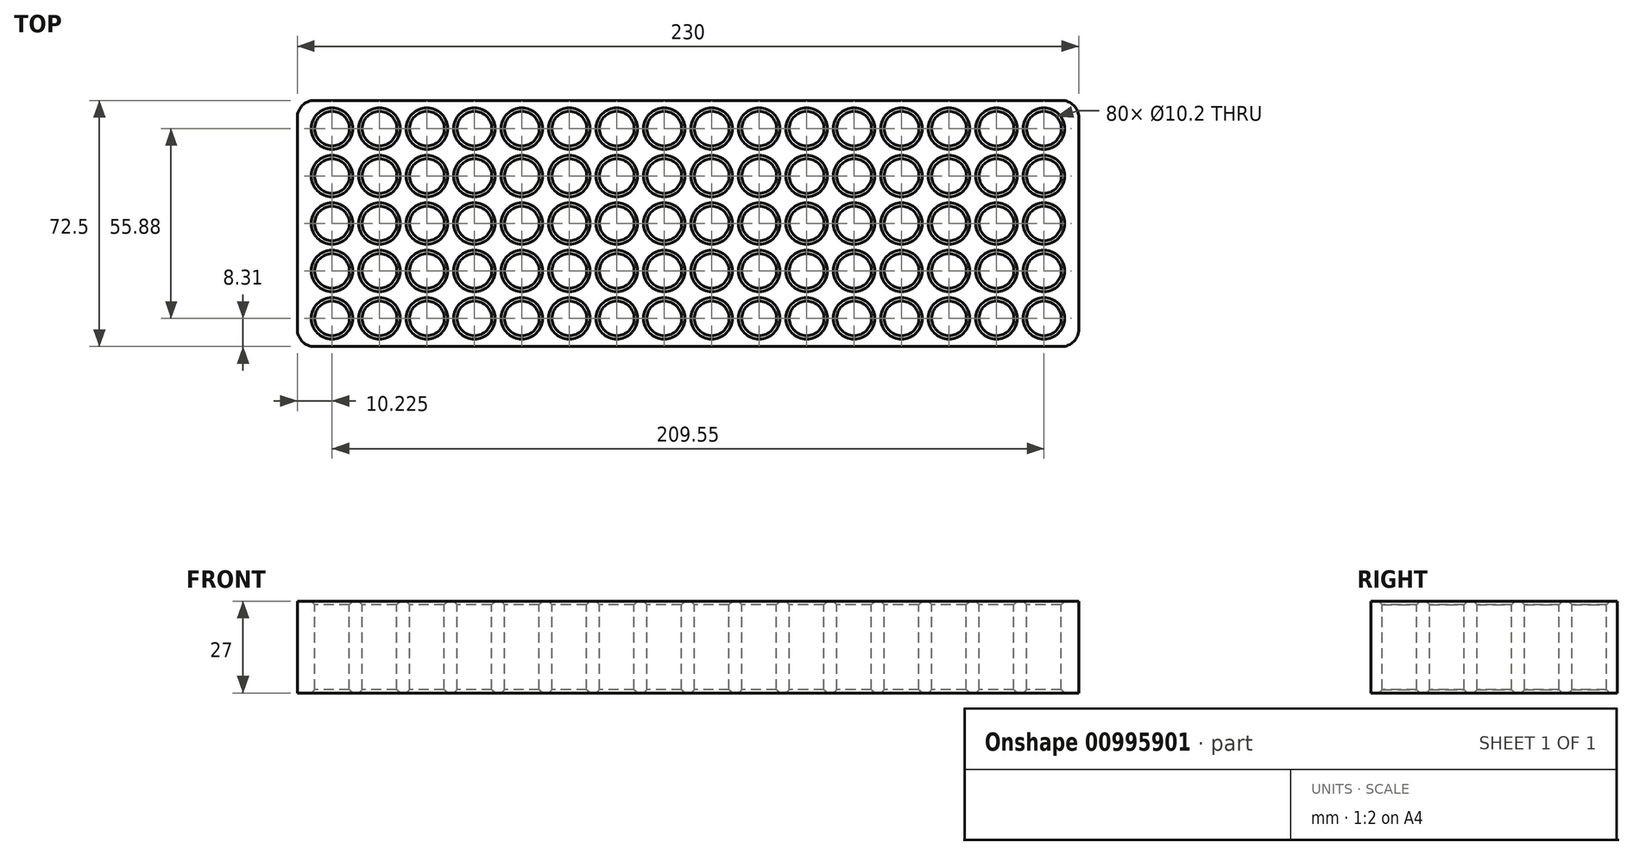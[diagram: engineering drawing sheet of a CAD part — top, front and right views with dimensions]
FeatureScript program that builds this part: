
annotation { "Feature Type Name" : "Feature", "Feature Type Description" : "" }
export const myFeature = defineFeature(function(context is Context, id is Id, definition is map)
    precondition{}
    {
        {
            var Q0;
            Q0=qCreatedBy(makeId("Top.planeOp"),FACE);
            var sketch = newSketch(context, id + "F0", { "sketchPlane" : qUnion([Q0])});
            skLineSegment(sketch, "E0.bottom", {"start": v(115, 36.25) * mm, "end": v(-115, 36.25) * mm});
            skLineSegment(sketch, "E0.top", {"start": v(115, -36.25) * mm, "end": v(-115, -36.25) * mm});
            skLineSegment(sketch, "E0.left", {"start": v(115, 36.25) * mm, "end": v(115, -36.25) * mm});
            skLineSegment(sketch, "E0.right", {"start": v(-115, 36.25) * mm, "end": v(-115, -36.25) * mm});
            skPoint(sketch, "E0.middle", {"position": v(0, 0) * mm});
            skSolve(sketch);
        }
        {
            var Q0;
            Q0=makeQuery(id+"F0.imprint","IMPRINT",FACE,{"disambiguationData":[TD([[makeQuery(id+"F0.imprint","IMPRINT",EDGE,{"derivedFrom":sQuery(id+"F0.wireOp",EDGE,"E0.bottom")}),1.0]])]});
            extrude(context, id + "F1", {"entities" : qUnion([Q0]), "endBound" : BoundingType.SYMMETRIC, "depth" : 27 * mm, "offsetDistance" : 25.4 * mm});
        }
        {
            var Q0;
            Q0=makeQuery(id+"F1.opExtrude","CAP_FACE",FACE,{"disambiguationData":[OSD([sQuery(id+"F0.wireOp",EDGE,"E0.bottom"),sQuery(id+"F0.wireOp",EDGE,"E0.top"),sQuery(id+"F0.wireOp",EDGE,"E0.left"),sQuery(id+"F0.wireOp",EDGE,"E0.right")])],"isStart":false});
            var sketch = newSketch(context, id + "F2", { "sketchPlane" : qUnion([Q0])});
            skCircle(sketch, "E1", {"center": v(-104.78, 27.94) * mm, "radius": 5.1 * mm});
            skCircle(sketch, "E2.0.1.0", {"center": v(-104.78, 13.97) * mm, "radius": 5.1 * mm});
            skCircle(sketch, "E2.0.2.0", {"center": v(-104.77, 0) * mm, "radius": 5.1 * mm});
            skCircle(sketch, "E2.0.3.0", {"center": v(-104.78, -13.97) * mm, "radius": 5.1 * mm});
            skCircle(sketch, "E2.0.4.0", {"center": v(-104.78, -27.94) * mm, "radius": 5.1 * mm});
            skCircle(sketch, "E2.1.0.0", {"center": v(-90.8, 27.94) * mm, "radius": 5.1 * mm});
            skCircle(sketch, "E2.1.1.0", {"center": v(-90.8, 13.97) * mm, "radius": 5.1 * mm});
            skCircle(sketch, "E2.1.2.0", {"center": v(-90.8, 0) * mm, "radius": 5.1 * mm});
            skCircle(sketch, "E2.1.3.0", {"center": v(-90.8, -13.97) * mm, "radius": 5.1 * mm});
            skCircle(sketch, "E2.1.4.0", {"center": v(-90.8, -27.94) * mm, "radius": 5.1 * mm});
            skCircle(sketch, "E2.2.0.0", {"center": v(-76.84, 27.94) * mm, "radius": 5.1 * mm});
            skCircle(sketch, "E2.2.1.0", {"center": v(-76.84, 13.97) * mm, "radius": 5.1 * mm});
            skCircle(sketch, "E2.2.2.0", {"center": v(-76.83, 0) * mm, "radius": 5.1 * mm});
            skCircle(sketch, "E2.2.3.0", {"center": v(-76.84, -13.97) * mm, "radius": 5.1 * mm});
            skCircle(sketch, "E2.2.4.0", {"center": v(-76.84, -27.94) * mm, "radius": 5.1 * mm});
            skCircle(sketch, "E2.3.0.0", {"center": v(-62.87, 27.94) * mm, "radius": 5.1 * mm});
            skCircle(sketch, "E2.3.1.0", {"center": v(-62.87, 13.97) * mm, "radius": 5.1 * mm});
            skCircle(sketch, "E2.3.2.0", {"center": v(-62.87, 0) * mm, "radius": 5.1 * mm});
            skCircle(sketch, "E2.3.3.0", {"center": v(-62.87, -13.97) * mm, "radius": 5.1 * mm});
            skCircle(sketch, "E2.3.4.0", {"center": v(-62.87, -27.94) * mm, "radius": 5.1 * mm});
            skCircle(sketch, "E2.4.0.0", {"center": v(-48.9, 27.94) * mm, "radius": 5.1 * mm});
            skCircle(sketch, "E2.4.1.0", {"center": v(-48.9, 13.97) * mm, "radius": 5.1 * mm});
            skCircle(sketch, "E2.4.2.0", {"center": v(-48.9, 0) * mm, "radius": 5.1 * mm});
            skCircle(sketch, "E2.4.3.0", {"center": v(-48.9, -13.97) * mm, "radius": 5.1 * mm});
            skCircle(sketch, "E2.4.4.0", {"center": v(-48.9, -27.94) * mm, "radius": 5.1 * mm});
            skCircle(sketch, "E2.5.0.0", {"center": v(-34.93, 27.94) * mm, "radius": 5.1 * mm});
            skCircle(sketch, "E2.5.1.0", {"center": v(-34.93, 13.97) * mm, "radius": 5.1 * mm});
            skCircle(sketch, "E2.5.2.0", {"center": v(-34.93, 0) * mm, "radius": 5.1 * mm});
            skCircle(sketch, "E2.5.3.0", {"center": v(-34.93, -13.97) * mm, "radius": 5.1 * mm});
            skCircle(sketch, "E2.5.4.0", {"center": v(-34.93, -27.94) * mm, "radius": 5.1 * mm});
            skCircle(sketch, "E2.6.0.0", {"center": v(-20.96, 27.94) * mm, "radius": 5.1 * mm});
            skCircle(sketch, "E2.6.1.0", {"center": v(-20.96, 13.97) * mm, "radius": 5.1 * mm});
            skCircle(sketch, "E2.6.2.0", {"center": v(-20.96, 0) * mm, "radius": 5.1 * mm});
            skCircle(sketch, "E2.6.3.0", {"center": v(-20.96, -13.97) * mm, "radius": 5.1 * mm});
            skCircle(sketch, "E2.6.4.0", {"center": v(-20.96, -27.94) * mm, "radius": 5.1 * mm});
            skCircle(sketch, "E2.7.0.0", {"center": v(-6.99, 27.94) * mm, "radius": 5.1 * mm});
            skCircle(sketch, "E2.7.1.0", {"center": v(-6.99, 13.97) * mm, "radius": 5.1 * mm});
            skCircle(sketch, "E2.7.2.0", {"center": v(-6.99, 0) * mm, "radius": 5.1 * mm});
            skCircle(sketch, "E2.7.3.0", {"center": v(-6.99, -13.97) * mm, "radius": 5.1 * mm});
            skCircle(sketch, "E2.7.4.0", {"center": v(-6.99, -27.94) * mm, "radius": 5.1 * mm});
            skCircle(sketch, "E2.8.0.0", {"center": v(6.98, 27.94) * mm, "radius": 5.1 * mm});
            skCircle(sketch, "E2.8.1.0", {"center": v(6.98, 13.97) * mm, "radius": 5.1 * mm});
            skCircle(sketch, "E2.8.2.0", {"center": v(6.98, 0) * mm, "radius": 5.1 * mm});
            skCircle(sketch, "E2.8.3.0", {"center": v(6.98, -13.97) * mm, "radius": 5.1 * mm});
            skCircle(sketch, "E2.8.4.0", {"center": v(6.98, -27.94) * mm, "radius": 5.1 * mm});
            skCircle(sketch, "E2.9.0.0", {"center": v(20.96, 27.94) * mm, "radius": 5.1 * mm});
            skCircle(sketch, "E2.9.1.0", {"center": v(20.96, 13.97) * mm, "radius": 5.1 * mm});
            skCircle(sketch, "E2.9.2.0", {"center": v(20.95, 0) * mm, "radius": 5.1 * mm});
            skCircle(sketch, "E2.9.3.0", {"center": v(20.96, -13.97) * mm, "radius": 5.1 * mm});
            skCircle(sketch, "E2.9.4.0", {"center": v(20.96, -27.94) * mm, "radius": 5.1 * mm});
            skCircle(sketch, "E2.10.0.0", {"center": v(34.93, 27.94) * mm, "radius": 5.1 * mm});
            skCircle(sketch, "E2.10.1.0", {"center": v(34.93, 13.97) * mm, "radius": 5.1 * mm});
            skCircle(sketch, "E2.10.2.0", {"center": v(34.92, 0) * mm, "radius": 5.1 * mm});
            skCircle(sketch, "E2.10.3.0", {"center": v(34.93, -13.97) * mm, "radius": 5.1 * mm});
            skCircle(sketch, "E2.10.4.0", {"center": v(34.93, -27.94) * mm, "radius": 5.1 * mm});
            skCircle(sketch, "E2.11.0.0", {"center": v(48.9, 27.94) * mm, "radius": 5.1 * mm});
            skCircle(sketch, "E2.11.1.0", {"center": v(48.9, 13.97) * mm, "radius": 5.1 * mm});
            skCircle(sketch, "E2.11.2.0", {"center": v(48.9, 0) * mm, "radius": 5.1 * mm});
            skCircle(sketch, "E2.11.3.0", {"center": v(48.9, -13.97) * mm, "radius": 5.1 * mm});
            skCircle(sketch, "E2.11.4.0", {"center": v(48.9, -27.94) * mm, "radius": 5.1 * mm});
            skCircle(sketch, "E2.12.0.0", {"center": v(62.87, 27.94) * mm, "radius": 5.1 * mm});
            skCircle(sketch, "E2.12.1.0", {"center": v(62.87, 13.97) * mm, "radius": 5.1 * mm});
            skCircle(sketch, "E2.12.2.0", {"center": v(62.86, 0) * mm, "radius": 5.1 * mm});
            skCircle(sketch, "E2.12.3.0", {"center": v(62.87, -13.97) * mm, "radius": 5.1 * mm});
            skCircle(sketch, "E2.12.4.0", {"center": v(62.87, -27.94) * mm, "radius": 5.1 * mm});
            skCircle(sketch, "E2.13.0.0", {"center": v(76.84, 27.94) * mm, "radius": 5.1 * mm});
            skCircle(sketch, "E2.13.1.0", {"center": v(76.84, 13.97) * mm, "radius": 5.1 * mm});
            skCircle(sketch, "E2.13.2.0", {"center": v(76.83, 0) * mm, "radius": 5.1 * mm});
            skCircle(sketch, "E2.13.3.0", {"center": v(76.84, -13.97) * mm, "radius": 5.1 * mm});
            skCircle(sketch, "E2.13.4.0", {"center": v(76.84, -27.94) * mm, "radius": 5.1 * mm});
            skCircle(sketch, "E2.14.0.0", {"center": v(90.8, 27.94) * mm, "radius": 5.1 * mm});
            skCircle(sketch, "E2.14.1.0", {"center": v(90.8, 13.97) * mm, "radius": 5.1 * mm});
            skCircle(sketch, "E2.14.2.0", {"center": v(90.8, 0) * mm, "radius": 5.1 * mm});
            skCircle(sketch, "E2.14.3.0", {"center": v(90.8, -13.97) * mm, "radius": 5.1 * mm});
            skCircle(sketch, "E2.14.4.0", {"center": v(90.8, -27.94) * mm, "radius": 5.1 * mm});
            skCircle(sketch, "E2.15.0.0", {"center": v(104.78, 27.94) * mm, "radius": 5.1 * mm});
            skCircle(sketch, "E2.15.1.0", {"center": v(104.78, 13.97) * mm, "radius": 5.1 * mm});
            skCircle(sketch, "E2.15.2.0", {"center": v(104.77, 0) * mm, "radius": 5.1 * mm});
            skCircle(sketch, "E2.15.3.0", {"center": v(104.78, -13.97) * mm, "radius": 5.1 * mm});
            skCircle(sketch, "E2.15.4.0", {"center": v(104.78, -27.94) * mm, "radius": 5.1 * mm});
            skLineSegment(sketch, "E2.direction1", {"start": v(-104.78, 27.94) * mm, "end": v(-90.8, 27.94) * mm, "construction": true});
            skLineSegment(sketch, "E2.direction2", {"start": v(-104.78, 27.94) * mm, "end": v(-104.78, 13.97) * mm, "construction": true});
            skSolve(sketch);
        }
        {
            var Q0;
            Q0 = qSketchRegion(id + "F2", true);
            extrude(context, id + "F3", {"entities" : qUnion([Q0]), "operationType" : NewBodyOperationType.REMOVE, "endBound" : BoundingType.THROUGH_ALL, "oppositeDirection" : true, "depth" : 25.4 * mm, "offsetDistance" : 25.4 * mm});
        }
        {
            var Q0;
            Q0=makeQuery(id+"F3.boolean.opBoolean","COPY",FACE,{"derivedFrom":makeQuery(id+"F3.opExtrude","SWEPT_FACE",FACE,{"disambiguationData":[OSD([sQuery(id+"F2.wireOp",EDGE,"E1")])]})});
            var Q1;
            Q1=makeQuery(id+"F3.boolean.opBoolean","COPY",FACE,{"derivedFrom":makeQuery(id+"F3.opExtrude","SWEPT_FACE",FACE,{"disambiguationData":[OSD([sQuery(id+"F2.wireOp",EDGE,"E2.0.1.0")])]})});
            var Q2;
            Q2=makeQuery(id+"F3.boolean.opBoolean","COPY",FACE,{"derivedFrom":makeQuery(id+"F3.opExtrude","SWEPT_FACE",FACE,{"disambiguationData":[OSD([sQuery(id+"F2.wireOp",EDGE,"E2.1.0.0")])]})});
            var Q3;
            Q3=makeQuery(id+"F3.boolean.opBoolean","COPY",FACE,{"derivedFrom":makeQuery(id+"F3.opExtrude","SWEPT_FACE",FACE,{"disambiguationData":[OSD([sQuery(id+"F2.wireOp",EDGE,"E2.1.1.0")])]})});
            var Q4;
            Q4=makeQuery(id+"F3.boolean.opBoolean","COPY",FACE,{"derivedFrom":makeQuery(id+"F3.opExtrude","SWEPT_FACE",FACE,{"disambiguationData":[OSD([sQuery(id+"F2.wireOp",EDGE,"E2.2.0.0")])]})});
            var Q5;
            Q5=makeQuery(id+"F3.boolean.opBoolean","COPY",FACE,{"derivedFrom":makeQuery(id+"F3.opExtrude","SWEPT_FACE",FACE,{"disambiguationData":[OSD([sQuery(id+"F2.wireOp",EDGE,"E2.3.0.0")])]})});
            var Q6;
            Q6=makeQuery(id+"F3.boolean.opBoolean","COPY",FACE,{"derivedFrom":makeQuery(id+"F3.opExtrude","SWEPT_FACE",FACE,{"disambiguationData":[OSD([sQuery(id+"F2.wireOp",EDGE,"E2.4.0.0")])]})});
            var Q7;
            Q7=makeQuery(id+"F3.boolean.opBoolean","COPY",FACE,{"derivedFrom":makeQuery(id+"F3.opExtrude","SWEPT_FACE",FACE,{"disambiguationData":[OSD([sQuery(id+"F2.wireOp",EDGE,"E2.2.1.0")])]})});
            var Q8;
            Q8=makeQuery(id+"F3.boolean.opBoolean","COPY",FACE,{"derivedFrom":makeQuery(id+"F3.opExtrude","SWEPT_FACE",FACE,{"disambiguationData":[OSD([sQuery(id+"F2.wireOp",EDGE,"E2.2.2.0")])]})});
            var Q9;
            Q9=makeQuery(id+"F3.boolean.opBoolean","COPY",FACE,{"derivedFrom":makeQuery(id+"F3.opExtrude","SWEPT_FACE",FACE,{"disambiguationData":[OSD([sQuery(id+"F2.wireOp",EDGE,"E2.2.3.0")])]})});
            var Q10;
            Q10=makeQuery(id+"F3.boolean.opBoolean","COPY",FACE,{"derivedFrom":makeQuery(id+"F3.opExtrude","SWEPT_FACE",FACE,{"disambiguationData":[OSD([sQuery(id+"F2.wireOp",EDGE,"E2.2.4.0")])]})});
            var Q11;
            Q11=makeQuery(id+"F3.boolean.opBoolean","COPY",FACE,{"derivedFrom":makeQuery(id+"F3.opExtrude","SWEPT_FACE",FACE,{"disambiguationData":[OSD([sQuery(id+"F2.wireOp",EDGE,"E2.3.4.0")])]})});
            var Q12;
            Q12=makeQuery(id+"F3.boolean.opBoolean","COPY",FACE,{"derivedFrom":makeQuery(id+"F3.opExtrude","SWEPT_FACE",FACE,{"disambiguationData":[OSD([sQuery(id+"F2.wireOp",EDGE,"E2.3.3.0")])]})});
            var Q13;
            Q13=makeQuery(id+"F3.boolean.opBoolean","COPY",FACE,{"derivedFrom":makeQuery(id+"F3.opExtrude","SWEPT_FACE",FACE,{"disambiguationData":[OSD([sQuery(id+"F2.wireOp",EDGE,"E2.3.2.0")])]})});
            var Q14;
            Q14=makeQuery(id+"F3.boolean.opBoolean","COPY",FACE,{"derivedFrom":makeQuery(id+"F3.opExtrude","SWEPT_FACE",FACE,{"disambiguationData":[OSD([sQuery(id+"F2.wireOp",EDGE,"E2.3.1.0")])]})});
            var Q15;
            Q15=makeQuery(id+"F3.boolean.opBoolean","COPY",FACE,{"derivedFrom":makeQuery(id+"F3.opExtrude","SWEPT_FACE",FACE,{"disambiguationData":[OSD([sQuery(id+"F2.wireOp",EDGE,"E2.4.2.0")])]})});
            var Q16;
            Q16=makeQuery(id+"F3.boolean.opBoolean","COPY",FACE,{"derivedFrom":makeQuery(id+"F3.opExtrude","SWEPT_FACE",FACE,{"disambiguationData":[OSD([sQuery(id+"F2.wireOp",EDGE,"E2.4.3.0")])]})});
            var Q17;
            Q17=makeQuery(id+"F3.boolean.opBoolean","COPY",FACE,{"derivedFrom":makeQuery(id+"F3.opExtrude","SWEPT_FACE",FACE,{"disambiguationData":[OSD([sQuery(id+"F2.wireOp",EDGE,"E2.4.4.0")])]})});
            var Q18;
            Q18=makeQuery(id+"F3.boolean.opBoolean","COPY",FACE,{"derivedFrom":makeQuery(id+"F3.opExtrude","SWEPT_FACE",FACE,{"disambiguationData":[OSD([sQuery(id+"F2.wireOp",EDGE,"E2.4.1.0")])]})});
            var Q19;
            Q19=makeQuery(id+"F3.boolean.opBoolean","COPY",FACE,{"derivedFrom":makeQuery(id+"F3.opExtrude","SWEPT_FACE",FACE,{"disambiguationData":[OSD([sQuery(id+"F2.wireOp",EDGE,"E2.5.1.0")])]})});
            var Q20;
            Q20=makeQuery(id+"F3.boolean.opBoolean","COPY",FACE,{"derivedFrom":makeQuery(id+"F3.opExtrude","SWEPT_FACE",FACE,{"disambiguationData":[OSD([sQuery(id+"F2.wireOp",EDGE,"E2.5.0.0")])]})});
            var Q21;
            Q21=makeQuery(id+"F3.boolean.opBoolean","COPY",EDGE,{"derivedFrom":makeQuery(id+"F3.opExtrude","CAP_EDGE",EDGE,{"disambiguationData":[OSD([sQuery(id+"F2.wireOp",EDGE,"E2.6.0.0")])],"isStart":true})});
            var Q22;
            Q22=makeQuery(id+"F3.boolean.opBoolean","COPY",FACE,{"derivedFrom":makeQuery(id+"F3.opExtrude","SWEPT_FACE",FACE,{"disambiguationData":[OSD([sQuery(id+"F2.wireOp",EDGE,"E2.6.1.0")])]})});
            var Q23;
            Q23=makeQuery(id+"F3.boolean.opBoolean","COPY",FACE,{"derivedFrom":makeQuery(id+"F3.opExtrude","SWEPT_FACE",FACE,{"disambiguationData":[OSD([sQuery(id+"F2.wireOp",EDGE,"E2.6.0.0")])]})});
            var Q24;
            Q24=makeQuery(id+"F3.boolean.opBoolean","COPY",FACE,{"derivedFrom":makeQuery(id+"F3.opExtrude","SWEPT_FACE",FACE,{"disambiguationData":[OSD([sQuery(id+"F2.wireOp",EDGE,"E2.6.2.0")])]})});
            var Q25;
            Q25=makeQuery(id+"F3.boolean.opBoolean","COPY",FACE,{"derivedFrom":makeQuery(id+"F3.opExtrude","SWEPT_FACE",FACE,{"disambiguationData":[OSD([sQuery(id+"F2.wireOp",EDGE,"E2.5.2.0")])]})});
            var Q26;
            Q26=makeQuery(id+"F3.boolean.opBoolean","COPY",FACE,{"derivedFrom":makeQuery(id+"F3.opExtrude","SWEPT_FACE",FACE,{"disambiguationData":[OSD([sQuery(id+"F2.wireOp",EDGE,"E2.5.3.0")])]})});
            var Q27;
            Q27=makeQuery(id+"F3.boolean.opBoolean","COPY",FACE,{"derivedFrom":makeQuery(id+"F3.opExtrude","SWEPT_FACE",FACE,{"disambiguationData":[OSD([sQuery(id+"F2.wireOp",EDGE,"E2.6.3.0")])]})});
            var Q28;
            Q28=makeQuery(id+"F3.boolean.opBoolean","COPY",FACE,{"derivedFrom":makeQuery(id+"F3.opExtrude","SWEPT_FACE",FACE,{"disambiguationData":[OSD([sQuery(id+"F2.wireOp",EDGE,"E2.5.4.0")])]})});
            var Q29;
            Q29=makeQuery(id+"F3.boolean.opBoolean","COPY",FACE,{"derivedFrom":makeQuery(id+"F3.opExtrude","SWEPT_FACE",FACE,{"disambiguationData":[OSD([sQuery(id+"F2.wireOp",EDGE,"E2.6.4.0")])]})});
            var Q30;
            Q30=makeQuery(id+"F3.boolean.opBoolean","COPY",FACE,{"derivedFrom":makeQuery(id+"F3.opExtrude","SWEPT_FACE",FACE,{"disambiguationData":[OSD([sQuery(id+"F2.wireOp",EDGE,"E2.7.4.0")])]})});
            var Q31;
            Q31=makeQuery(id+"F3.boolean.opBoolean","COPY",FACE,{"derivedFrom":makeQuery(id+"F3.opExtrude","SWEPT_FACE",FACE,{"disambiguationData":[OSD([sQuery(id+"F2.wireOp",EDGE,"E2.7.3.0")])]})});
            var Q32;
            Q32=makeQuery(id+"F3.boolean.opBoolean","COPY",FACE,{"derivedFrom":makeQuery(id+"F3.opExtrude","SWEPT_FACE",FACE,{"disambiguationData":[OSD([sQuery(id+"F2.wireOp",EDGE,"E2.7.2.0")])]})});
            var Q33;
            Q33=makeQuery(id+"F3.boolean.opBoolean","COPY",FACE,{"derivedFrom":makeQuery(id+"F3.opExtrude","SWEPT_FACE",FACE,{"disambiguationData":[OSD([sQuery(id+"F2.wireOp",EDGE,"E2.7.1.0")])]})});
            var Q34;
            Q34=makeQuery(id+"F3.boolean.opBoolean","COPY",FACE,{"derivedFrom":makeQuery(id+"F3.opExtrude","SWEPT_FACE",FACE,{"disambiguationData":[OSD([sQuery(id+"F2.wireOp",EDGE,"E2.7.0.0")])]})});
            var Q35;
            Q35=makeQuery(id+"F3.boolean.opBoolean","COPY",FACE,{"derivedFrom":makeQuery(id+"F3.opExtrude","SWEPT_FACE",FACE,{"disambiguationData":[OSD([sQuery(id+"F2.wireOp",EDGE,"E2.8.0.0")])]})});
            var Q36;
            Q36=makeQuery(id+"F3.boolean.opBoolean","COPY",FACE,{"derivedFrom":makeQuery(id+"F3.opExtrude","SWEPT_FACE",FACE,{"disambiguationData":[OSD([sQuery(id+"F2.wireOp",EDGE,"E2.8.1.0")])]})});
            var Q37;
            Q37=makeQuery(id+"F3.boolean.opBoolean","COPY",FACE,{"derivedFrom":makeQuery(id+"F3.opExtrude","SWEPT_FACE",FACE,{"disambiguationData":[OSD([sQuery(id+"F2.wireOp",EDGE,"E2.8.2.0")])]})});
            var Q38;
            Q38=makeQuery(id+"F3.boolean.opBoolean","COPY",FACE,{"derivedFrom":makeQuery(id+"F3.opExtrude","SWEPT_FACE",FACE,{"disambiguationData":[OSD([sQuery(id+"F2.wireOp",EDGE,"E2.8.3.0")])]})});
            var Q39;
            Q39=makeQuery(id+"F3.boolean.opBoolean","COPY",FACE,{"derivedFrom":makeQuery(id+"F3.opExtrude","SWEPT_FACE",FACE,{"disambiguationData":[OSD([sQuery(id+"F2.wireOp",EDGE,"E2.8.4.0")])]})});
            var Q40;
            Q40=makeQuery(id+"F3.boolean.opBoolean","COPY",FACE,{"derivedFrom":makeQuery(id+"F3.opExtrude","SWEPT_FACE",FACE,{"disambiguationData":[OSD([sQuery(id+"F2.wireOp",EDGE,"E2.9.4.0")])]})});
            var Q41;
            Q41=makeQuery(id+"F3.boolean.opBoolean","COPY",FACE,{"derivedFrom":makeQuery(id+"F3.opExtrude","SWEPT_FACE",FACE,{"disambiguationData":[OSD([sQuery(id+"F2.wireOp",EDGE,"E2.9.3.0")])]})});
            var Q42;
            Q42=makeQuery(id+"F3.boolean.opBoolean","COPY",FACE,{"derivedFrom":makeQuery(id+"F3.opExtrude","SWEPT_FACE",FACE,{"disambiguationData":[OSD([sQuery(id+"F2.wireOp",EDGE,"E2.9.2.0")])]})});
            var Q43;
            Q43=makeQuery(id+"F3.boolean.opBoolean","COPY",FACE,{"derivedFrom":makeQuery(id+"F3.opExtrude","SWEPT_FACE",FACE,{"disambiguationData":[OSD([sQuery(id+"F2.wireOp",EDGE,"E2.9.1.0")])]})});
            var Q44;
            Q44=makeQuery(id+"F3.boolean.opBoolean","COPY",FACE,{"derivedFrom":makeQuery(id+"F3.opExtrude","SWEPT_FACE",FACE,{"disambiguationData":[OSD([sQuery(id+"F2.wireOp",EDGE,"E2.9.0.0")])]})});
            var Q45;
            Q45=makeQuery(id+"F3.boolean.opBoolean","COPY",FACE,{"derivedFrom":makeQuery(id+"F3.opExtrude","SWEPT_FACE",FACE,{"disambiguationData":[OSD([sQuery(id+"F2.wireOp",EDGE,"E2.10.0.0")])]})});
            var Q46;
            Q46=makeQuery(id+"F3.boolean.opBoolean","COPY",FACE,{"derivedFrom":makeQuery(id+"F3.opExtrude","SWEPT_FACE",FACE,{"disambiguationData":[OSD([sQuery(id+"F2.wireOp",EDGE,"E2.10.1.0")])]})});
            var Q47;
            Q47=makeQuery(id+"F3.boolean.opBoolean","COPY",FACE,{"derivedFrom":makeQuery(id+"F3.opExtrude","SWEPT_FACE",FACE,{"disambiguationData":[OSD([sQuery(id+"F2.wireOp",EDGE,"E2.11.0.0")])]})});
            var Q48;
            Q48=makeQuery(id+"F3.boolean.opBoolean","COPY",FACE,{"derivedFrom":makeQuery(id+"F3.opExtrude","SWEPT_FACE",FACE,{"disambiguationData":[OSD([sQuery(id+"F2.wireOp",EDGE,"E2.11.1.0")])]})});
            var Q49;
            Q49=makeQuery(id+"F3.boolean.opBoolean","COPY",FACE,{"derivedFrom":makeQuery(id+"F3.opExtrude","SWEPT_FACE",FACE,{"disambiguationData":[OSD([sQuery(id+"F2.wireOp",EDGE,"E2.11.2.0")])]})});
            var Q50;
            Q50=makeQuery(id+"F3.boolean.opBoolean","COPY",FACE,{"derivedFrom":makeQuery(id+"F3.opExtrude","SWEPT_FACE",FACE,{"disambiguationData":[OSD([sQuery(id+"F2.wireOp",EDGE,"E2.10.2.0")])]})});
            var Q51;
            Q51=makeQuery(id+"F3.boolean.opBoolean","COPY",FACE,{"derivedFrom":makeQuery(id+"F3.opExtrude","SWEPT_FACE",FACE,{"disambiguationData":[OSD([sQuery(id+"F2.wireOp",EDGE,"E2.10.3.0")])]})});
            var Q52;
            Q52=makeQuery(id+"F3.boolean.opBoolean","COPY",FACE,{"derivedFrom":makeQuery(id+"F3.opExtrude","SWEPT_FACE",FACE,{"disambiguationData":[OSD([sQuery(id+"F2.wireOp",EDGE,"E2.11.3.0")])]})});
            var Q53;
            Q53=makeQuery(id+"F3.boolean.opBoolean","COPY",FACE,{"derivedFrom":makeQuery(id+"F3.opExtrude","SWEPT_FACE",FACE,{"disambiguationData":[OSD([sQuery(id+"F2.wireOp",EDGE,"E2.11.4.0")])]})});
            var Q54;
            Q54=makeQuery(id+"F3.boolean.opBoolean","COPY",FACE,{"derivedFrom":makeQuery(id+"F3.opExtrude","SWEPT_FACE",FACE,{"disambiguationData":[OSD([sQuery(id+"F2.wireOp",EDGE,"E2.10.4.0")])]})});
            var Q55;
            Q55=makeQuery(id+"F3.boolean.opBoolean","COPY",FACE,{"derivedFrom":makeQuery(id+"F3.opExtrude","SWEPT_FACE",FACE,{"disambiguationData":[OSD([sQuery(id+"F2.wireOp",EDGE,"E2.12.4.0")])]})});
            var Q56;
            Q56=makeQuery(id+"F3.boolean.opBoolean","COPY",FACE,{"derivedFrom":makeQuery(id+"F3.opExtrude","SWEPT_FACE",FACE,{"disambiguationData":[OSD([sQuery(id+"F2.wireOp",EDGE,"E2.12.3.0")])]})});
            var Q57;
            Q57=makeQuery(id+"F3.boolean.opBoolean","COPY",FACE,{"derivedFrom":makeQuery(id+"F3.opExtrude","SWEPT_FACE",FACE,{"disambiguationData":[OSD([sQuery(id+"F2.wireOp",EDGE,"E2.12.2.0")])]})});
            var Q58;
            Q58=makeQuery(id+"F3.boolean.opBoolean","COPY",FACE,{"derivedFrom":makeQuery(id+"F3.opExtrude","SWEPT_FACE",FACE,{"disambiguationData":[OSD([sQuery(id+"F2.wireOp",EDGE,"E2.12.1.0")])]})});
            var Q59;
            Q59=makeQuery(id+"F3.boolean.opBoolean","COPY",FACE,{"derivedFrom":makeQuery(id+"F3.opExtrude","SWEPT_FACE",FACE,{"disambiguationData":[OSD([sQuery(id+"F2.wireOp",EDGE,"E2.12.0.0")])]})});
            var Q60;
            Q60=makeQuery(id+"F3.boolean.opBoolean","COPY",FACE,{"derivedFrom":makeQuery(id+"F3.opExtrude","SWEPT_FACE",FACE,{"disambiguationData":[OSD([sQuery(id+"F2.wireOp",EDGE,"E2.0.4.0")])]})});
            var Q61;
            Q61=makeQuery(id+"F3.boolean.opBoolean","COPY",FACE,{"derivedFrom":makeQuery(id+"F3.opExtrude","SWEPT_FACE",FACE,{"disambiguationData":[OSD([sQuery(id+"F2.wireOp",EDGE,"E2.1.4.0")])]})});
            var Q62;
            Q62=makeQuery(id+"F3.boolean.opBoolean","COPY",FACE,{"derivedFrom":makeQuery(id+"F3.opExtrude","SWEPT_FACE",FACE,{"disambiguationData":[OSD([sQuery(id+"F2.wireOp",EDGE,"E2.1.3.0")])]})});
            var Q63;
            Q63=makeQuery(id+"F3.boolean.opBoolean","COPY",FACE,{"derivedFrom":makeQuery(id+"F3.opExtrude","SWEPT_FACE",FACE,{"disambiguationData":[OSD([sQuery(id+"F2.wireOp",EDGE,"E2.0.3.0")])]})});
            var Q64;
            Q64=makeQuery(id+"F3.boolean.opBoolean","COPY",FACE,{"derivedFrom":makeQuery(id+"F3.opExtrude","SWEPT_FACE",FACE,{"disambiguationData":[OSD([sQuery(id+"F2.wireOp",EDGE,"E2.0.2.0")])]})});
            var Q65;
            Q65=makeQuery(id+"F3.boolean.opBoolean","COPY",FACE,{"derivedFrom":makeQuery(id+"F3.opExtrude","SWEPT_FACE",FACE,{"disambiguationData":[OSD([sQuery(id+"F2.wireOp",EDGE,"E2.1.2.0")])]})});
            var Q66;
            Q66=makeQuery(id+"F3.boolean.opBoolean","COPY",FACE,{"derivedFrom":makeQuery(id+"F3.opExtrude","SWEPT_FACE",FACE,{"disambiguationData":[OSD([sQuery(id+"F2.wireOp",EDGE,"E2.15.4.0")])]})});
            var Q67;
            Q67=makeQuery(id+"F3.boolean.opBoolean","COPY",FACE,{"derivedFrom":makeQuery(id+"F3.opExtrude","SWEPT_FACE",FACE,{"disambiguationData":[OSD([sQuery(id+"F2.wireOp",EDGE,"E2.14.4.0")])]})});
            var Q68;
            Q68=makeQuery(id+"F3.boolean.opBoolean","COPY",FACE,{"derivedFrom":makeQuery(id+"F3.opExtrude","SWEPT_FACE",FACE,{"disambiguationData":[OSD([sQuery(id+"F2.wireOp",EDGE,"E2.13.4.0")])]})});
            var Q69;
            Q69=makeQuery(id+"F3.boolean.opBoolean","COPY",FACE,{"derivedFrom":makeQuery(id+"F3.opExtrude","SWEPT_FACE",FACE,{"disambiguationData":[OSD([sQuery(id+"F2.wireOp",EDGE,"E2.13.3.0")])]})});
            var Q70;
            Q70=makeQuery(id+"F3.boolean.opBoolean","COPY",FACE,{"derivedFrom":makeQuery(id+"F3.opExtrude","SWEPT_FACE",FACE,{"disambiguationData":[OSD([sQuery(id+"F2.wireOp",EDGE,"E2.14.3.0")])]})});
            var Q71;
            Q71=makeQuery(id+"F3.boolean.opBoolean","COPY",FACE,{"derivedFrom":makeQuery(id+"F3.opExtrude","SWEPT_FACE",FACE,{"disambiguationData":[OSD([sQuery(id+"F2.wireOp",EDGE,"E2.15.3.0")])]})});
            var Q72;
            Q72=makeQuery(id+"F3.boolean.opBoolean","COPY",FACE,{"derivedFrom":makeQuery(id+"F3.opExtrude","SWEPT_FACE",FACE,{"disambiguationData":[OSD([sQuery(id+"F2.wireOp",EDGE,"E2.15.2.0")])]})});
            var Q73;
            Q73=makeQuery(id+"F3.boolean.opBoolean","COPY",FACE,{"derivedFrom":makeQuery(id+"F3.opExtrude","SWEPT_FACE",FACE,{"disambiguationData":[OSD([sQuery(id+"F2.wireOp",EDGE,"E2.14.2.0")])]})});
            var Q74;
            Q74=makeQuery(id+"F3.boolean.opBoolean","COPY",EDGE,{"derivedFrom":makeQuery(id+"F3.opExtrude","CAP_EDGE",EDGE,{"disambiguationData":[OSD([sQuery(id+"F2.wireOp",EDGE,"E2.13.2.0")])],"isStart":true})});
            var Q75;
            Q75=makeQuery(id+"F3.boolean.opBoolean","COPY",FACE,{"derivedFrom":makeQuery(id+"F3.opExtrude","SWEPT_FACE",FACE,{"disambiguationData":[OSD([sQuery(id+"F2.wireOp",EDGE,"E2.13.1.0")])]})});
            var Q76;
            Q76=makeQuery(id+"F3.boolean.opBoolean","COPY",FACE,{"derivedFrom":makeQuery(id+"F3.opExtrude","SWEPT_FACE",FACE,{"disambiguationData":[OSD([sQuery(id+"F2.wireOp",EDGE,"E2.13.0.0")])]})});
            var Q77;
            Q77=makeQuery(id+"F3.boolean.opBoolean","COPY",FACE,{"derivedFrom":makeQuery(id+"F3.opExtrude","SWEPT_FACE",FACE,{"disambiguationData":[OSD([sQuery(id+"F2.wireOp",EDGE,"E2.14.0.0")])]})});
            var Q78;
            Q78=makeQuery(id+"F3.boolean.opBoolean","COPY",FACE,{"derivedFrom":makeQuery(id+"F3.opExtrude","SWEPT_FACE",FACE,{"disambiguationData":[OSD([sQuery(id+"F2.wireOp",EDGE,"E2.14.1.0")])]})});
            var Q79;
            Q79=makeQuery(id+"F3.boolean.opBoolean","COPY",EDGE,{"derivedFrom":makeQuery(id+"F3.opExtrude","CAP_EDGE",EDGE,{"disambiguationData":[OSD([sQuery(id+"F2.wireOp",EDGE,"E2.15.1.0")])],"isStart":true})});
            var Q80;
            Q80=makeQuery(id+"F3.boolean.opBoolean","COPY",FACE,{"derivedFrom":makeQuery(id+"F3.opExtrude","SWEPT_FACE",FACE,{"disambiguationData":[OSD([sQuery(id+"F2.wireOp",EDGE,"E2.13.2.0")])]})});
            var Q81;
            Q81=makeQuery(id+"F3.boolean.opBoolean","COPY",FACE,{"derivedFrom":makeQuery(id+"F3.opExtrude","SWEPT_FACE",FACE,{"disambiguationData":[OSD([sQuery(id+"F2.wireOp",EDGE,"E2.15.0.0")])]})});
            var Q82;
            Q82=makeQuery(id+"F3.boolean.opBoolean","COPY",FACE,{"derivedFrom":makeQuery(id+"F3.opExtrude","SWEPT_FACE",FACE,{"disambiguationData":[OSD([sQuery(id+"F2.wireOp",EDGE,"E2.15.1.0")])]})});
            chamfer(context, id + "F4", {"entities" : qUnion([Q0, Q1, Q2, Q3, Q4, Q5, Q6, Q7, Q8, Q9, Q10, Q11, Q12, Q13, Q14, Q15, Q16, Q17, Q18, Q19, Q20, Q21, Q22, Q23, Q24, Q25, Q26, Q27, Q28, Q29, Q30, Q31, Q32, Q33, Q34, Q35, Q36, Q37, Q38, Q39, Q40, Q41, Q42, Q43, Q44, Q45, Q46, Q47, Q48, Q49, Q50, Q51, Q52, Q53, Q54, Q55, Q56, Q57, Q58, Q59, Q60, Q61, Q62, Q63, Q64, Q65, Q66, Q67, Q68, Q69, Q70, Q71, Q72, Q73, Q74, Q75, Q76, Q77, Q78, Q79, Q80, Q81, Q82]), "width" : 1 * mm, "tangentPropagation" : true});
        }
        {
            var Q0;
            Q0=makeQuery(id+"F1.opExtrude","SWEPT_EDGE",EDGE,{"disambiguationData":[OSD([sQuery(id+"F0.wireOp",EDGE,"E0.top"),sQuery(id+"F0.wireOp",EDGE,"E0.right")])]});
            var Q1;
            Q1=makeQuery(id+"F1.opExtrude","SWEPT_EDGE",EDGE,{"disambiguationData":[OSD([sQuery(id+"F0.wireOp",EDGE,"E0.top"),sQuery(id+"F0.wireOp",EDGE,"E0.left")])]});
            var Q2;
            Q2=makeQuery(id+"F1.opExtrude","SWEPT_EDGE",EDGE,{"disambiguationData":[OSD([sQuery(id+"F0.wireOp",EDGE,"E0.bottom"),sQuery(id+"F0.wireOp",EDGE,"E0.left")])]});
            var Q3;
            Q3=makeQuery(id+"F1.opExtrude","SWEPT_EDGE",EDGE,{"disambiguationData":[OSD([sQuery(id+"F0.wireOp",EDGE,"E0.bottom"),sQuery(id+"F0.wireOp",EDGE,"E0.right")])]});
            fillet(context, id + "F5", {"entities" : qUnion([Q0, Q1, Q2, Q3]), "radius" : 5.08 * mm, "tangentPropagation" : true, "allowEdgeOverflow" : false});
        }
    });
